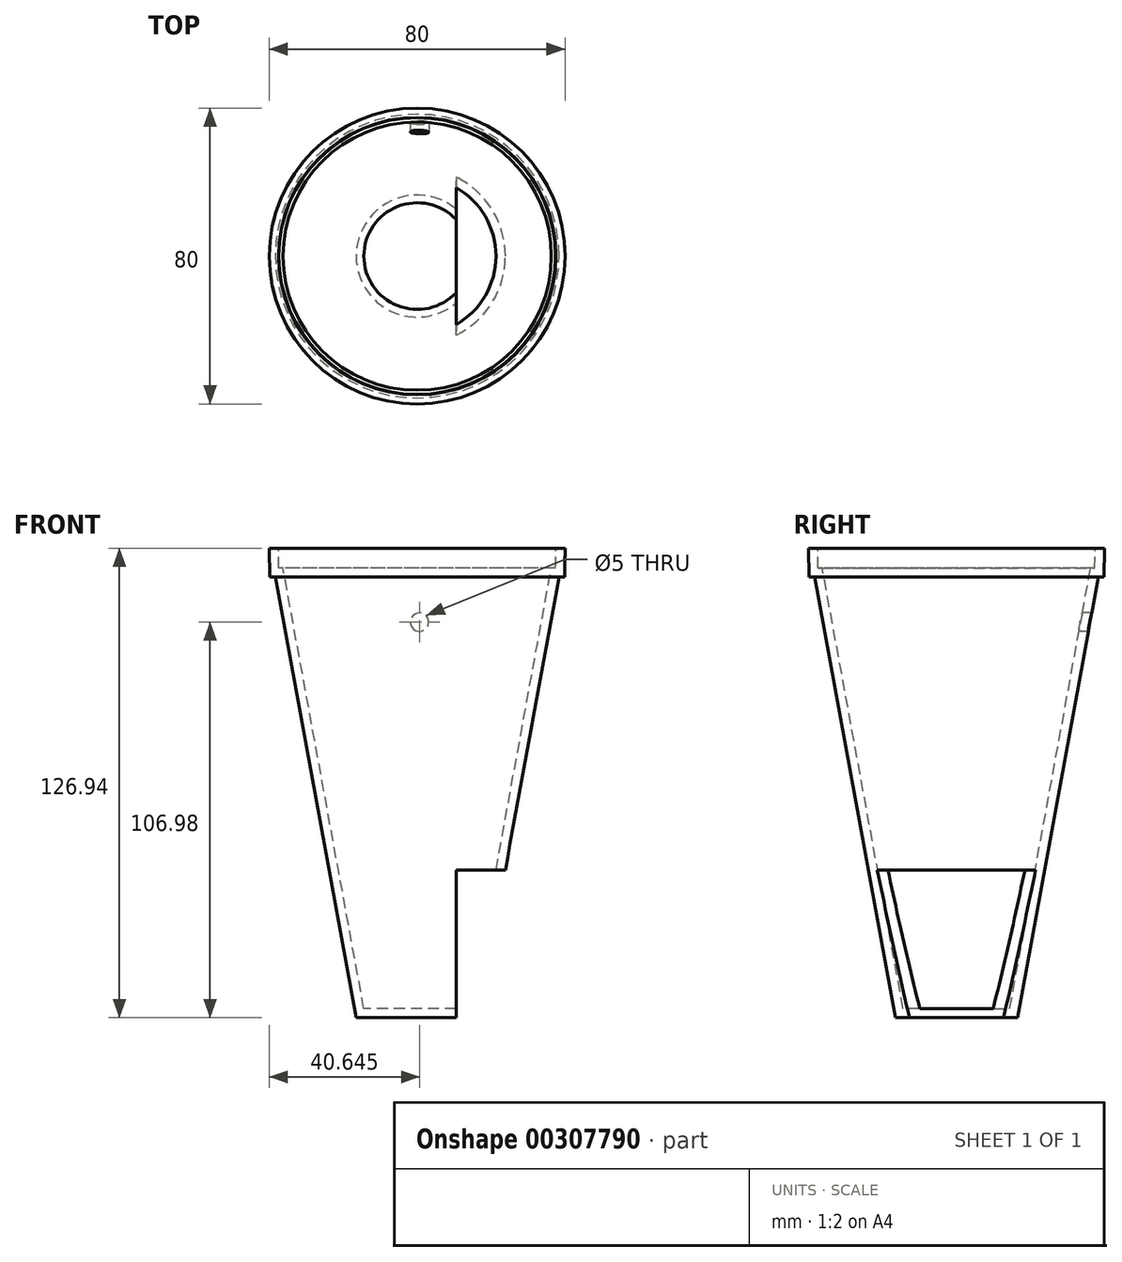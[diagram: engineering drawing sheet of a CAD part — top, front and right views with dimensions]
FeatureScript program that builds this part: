
annotation { "Feature Type Name" : "Feature", "Feature Type Description" : "" }
export const myFeature = defineFeature(function(context is Context, id is Id, definition is map)
    precondition{}
    {
        {
            var Q0;
            Q0=qCreatedBy(makeId("Front.planeOp"),FACE);
            var sketch = newSketch(context, id + "F0", { "sketchPlane" : qUnion([Q0])});
            skLineSegment(sketch, "E0", {"start": v(-26.34, -126.98) * mm, "end": v(-9.84, -126.98) * mm});
            skLineSegment(sketch, "E1", {"start": v(-26.34, 0.02) * mm, "end": v(-26.34, -126.98) * mm});
            skLineSegment(sketch, "E2", {"start": v(13.66, -0.04) * mm, "end": v(-26.34, 0.02) * mm});
            skLineSegment(sketch, "E3", {"start": v(-9.84, -126.98) * mm, "end": v(12.02, -7.87) * mm});
            skLineSegment(sketch, "E4", {"start": v(12.02, -7.87) * mm, "end": v(13.52, -7.87) * mm});
            skLineSegment(sketch, "E5", {"start": v(13.52, -7.87) * mm, "end": v(13.66, -0.04) * mm});
            skSolve(sketch);
        }
        {
            var Q0;
            Q0=makeQuery(id+"F0.imprint","IMPRINT",FACE,{"disambiguationData":[TD([[makeQuery(id+"F0.imprint","IMPRINT",EDGE,{"derivedFrom":sQuery(id+"F0.wireOp",EDGE,"E0")}),1.0]])]});
            var Q1;
            Q1=sQuery(id+"F0.wireOp",EDGE,"E1");
            revolve(context, id + "F1", {"entities" : qUnion([Q0]), "axis" : qUnion([Q1]), "revolveType" : RevolveType.FULL});
        }
        {
            var Q0;
            Q0=makeQuery(id+"F1.opRevolve","SWEPT_FACE",FACE,{"disambiguationData":[OSD([sQuery(id+"F0.wireOp",EDGE,"E2")])]});
            shell(context, id + "F2", {"entities" : qUnion([Q0]), "thickness" : 2.5 * mm});
        }
        {
            var Q0;
            Q0=qCreatedBy(makeId("Front.planeOp"),FACE);
            var sketch = newSketch(context, id + "F3", { "sketchPlane" : qUnion([Q0])});
            skLineSegment(sketch, "E6.bottom", {"start": v(-15.82, -130.35) * mm, "end": v(7.42, -130.35) * mm});
            skLineSegment(sketch, "E6.top", {"start": v(-15.82, -87) * mm, "end": v(7.42, -87) * mm});
            skLineSegment(sketch, "E6.left", {"start": v(-15.82, -130.35) * mm, "end": v(-15.82, -87) * mm});
            skLineSegment(sketch, "E6.right", {"start": v(7.42, -130.35) * mm, "end": v(7.42, -87) * mm});
            skPoint(sketch, "E7", {"position": v(-25.7, -20) * mm});
            skCircle(sketch, "E8", {"center": v(-25.7, -20) * mm, "radius": 2.5 * mm});
            skSolve(sketch);
        }
        {
            var Q0;
            Q0 = qSketchRegion(id + "F3", true);
            extrude(context, id + "F4", {"entities" : qUnion([Q0]), "operationType" : NewBodyOperationType.REMOVE, "endBound" : BoundingType.THROUGH_ALL, "oppositeDirection" : true, "depth" : 25 * mm});
        }
        {
            var Q0;
            Q0=makeQuery(id+"F3.imprint","IMPRINT",FACE,{"disambiguationData":[TD([[makeQuery(id+"F3.imprint","IMPRINT",EDGE,{"derivedFrom":sQuery(id+"F3.wireOp",EDGE,"E6.bottom")}),1.0]])]});
            extrude(context, id + "F5", {"entities" : qUnion([Q0]), "operationType" : NewBodyOperationType.REMOVE, "endBound" : BoundingType.THROUGH_ALL, "depth" : 25 * mm});
        }
    });
